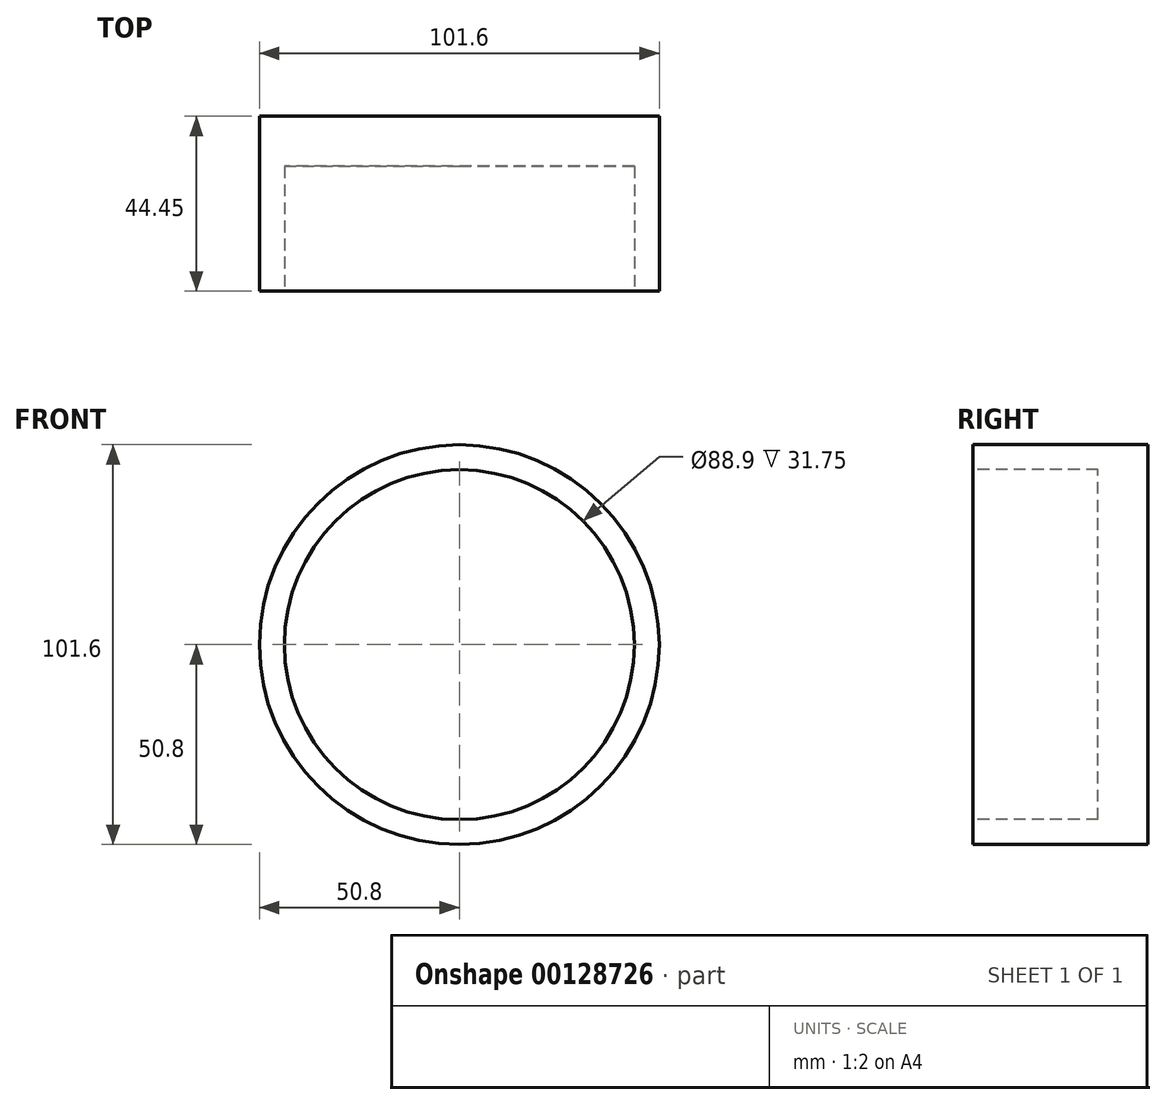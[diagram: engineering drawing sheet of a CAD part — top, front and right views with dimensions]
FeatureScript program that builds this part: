
annotation { "Feature Type Name" : "Feature", "Feature Type Description" : "" }
export const myFeature = defineFeature(function(context is Context, id is Id, definition is map)
    precondition{}
    {
        {
            var Q0;
            Q0=qCreatedBy(makeId("Front.planeOp"),FACE);
            var sketch = newSketch(context, id + "F0", { "sketchPlane" : qUnion([Q0])});
            skCircle(sketch, "E0", {"center": v(0, 0) * mm, "radius": 50.8 * mm});
            skSolve(sketch);
        }
        {
            var Q0;
            Q0=makeQuery(id+"F0.imprint","IMPRINT",FACE,{"disambiguationData":[TD([[makeQuery(id+"F0.imprint","IMPRINT",EDGE,{"derivedFrom":sQuery(id+"F0.wireOp",EDGE,"E0")}),1.0]])]});
            extrude(context, id + "F1", {"entities" : qUnion([Q0]), "depth" : 44.45 * mm});
        }
        {
            var Q0;
            Q0=makeQuery(id+"F1.opExtrude","CAP_FACE",FACE,{"disambiguationData":[OSD([sQuery(id+"F0.wireOp",EDGE,"E0")])],"isStart":false});
            var sketch = newSketch(context, id + "F2", { "sketchPlane" : qUnion([Q0])});
            skSolve(sketch);
        }
        {
            var Q0;
            Q0=makeQuery(id+"F2.imprint","IMPRINT",FACE,{"disambiguationData":[TD([[makeQuery(id+"F2.imprint","IMPRINT",EDGE,{"derivedFrom":makeQuery(id+"F1.opExtrude","CAP_EDGE",EDGE,{"disambiguationData":[OSD([sQuery(id+"F0.wireOp",EDGE,"E0")])],"isStart":false})}),1.0]])]});
            var sketch = newSketch(context, id + "F3", { "sketchPlane" : qUnion([Q0])});
            skCircle(sketch, "E1", {"center": v(0, 0) * mm, "radius": 44.45 * mm});
            skSolve(sketch);
        }
        {
            var Q0;
            Q0=makeQuery(id+"F3.imprint","IMPRINT",FACE,{"disambiguationData":[TD([[makeQuery(id+"F3.imprint","IMPRINT",EDGE,{"derivedFrom":sQuery(id+"F3.wireOp",EDGE,"E1")}),1.0]])]});
            extrude(context, id + "F4", {"entities" : qUnion([Q0]), "operationType" : NewBodyOperationType.REMOVE, "oppositeDirection" : true, "depth" : 31.75 * mm});
        }
    });
